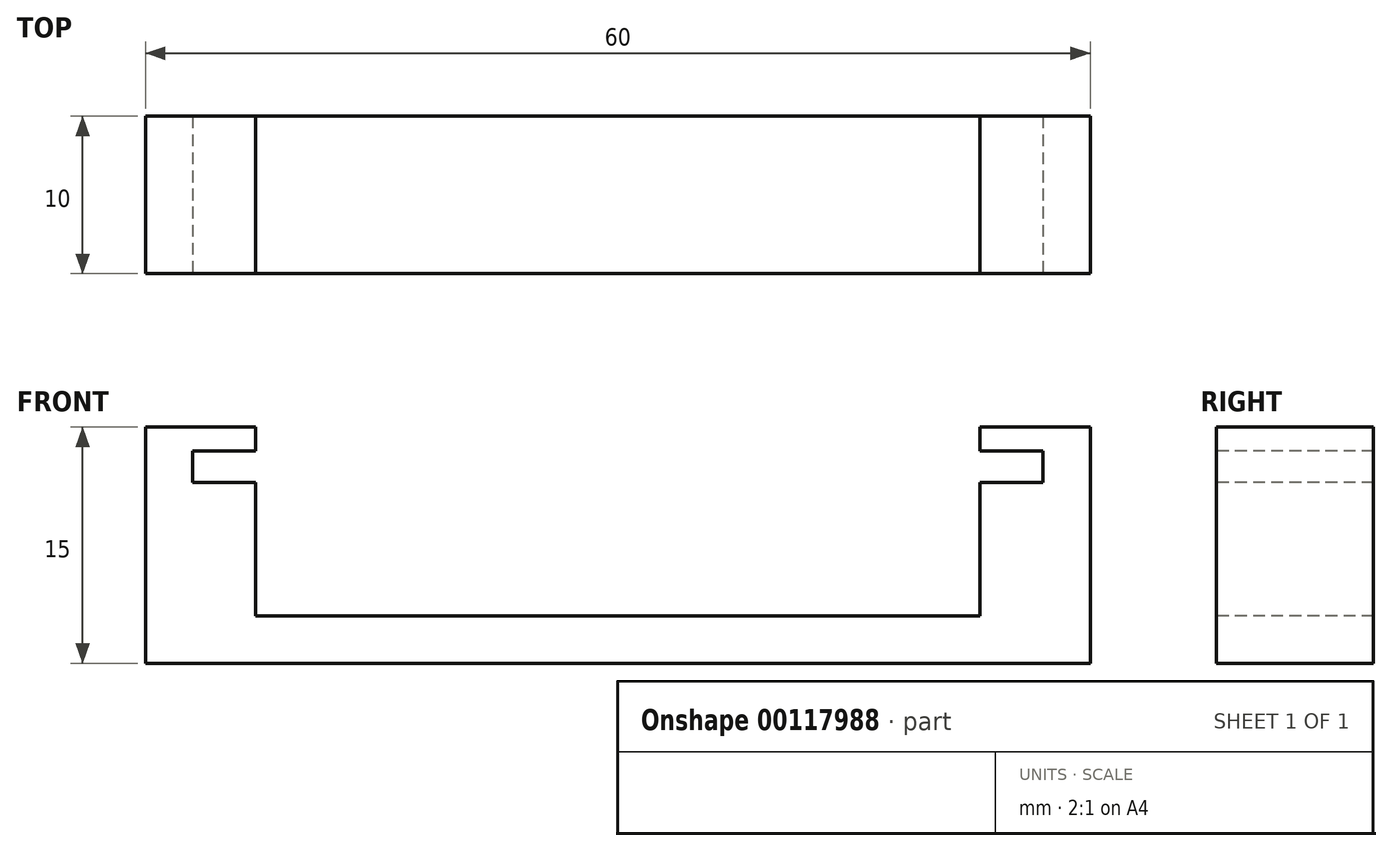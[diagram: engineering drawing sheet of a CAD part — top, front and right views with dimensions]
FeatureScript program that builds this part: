
annotation { "Feature Type Name" : "Feature", "Feature Type Description" : "" }
export const myFeature = defineFeature(function(context is Context, id is Id, definition is map)
    precondition{}
    {
        {
            var Q0;
            Q0=qCreatedBy(makeId("Top.planeOp"),FACE);
            var sketch = newSketch(context, id + "F0", { "sketchPlane" : qUnion([Q0])});
            skLineSegment(sketch, "E0.bottom", {"start": v(30, 5) * mm, "end": v(-30, 5) * mm});
            skLineSegment(sketch, "E0.top", {"start": v(30, -5) * mm, "end": v(-30, -5) * mm});
            skLineSegment(sketch, "E0.left", {"start": v(30, 5) * mm, "end": v(30, -5) * mm});
            skLineSegment(sketch, "E0.right", {"start": v(-30, 5) * mm, "end": v(-30, -5) * mm});
            skPoint(sketch, "E0.middle", {"position": v(0, 0) * mm});
            skSolve(sketch);
        }
        {
            var Q0;
            Q0=makeQuery(id+"F0.imprint","IMPRINT",FACE,{"disambiguationData":[TD([[makeQuery(id+"F0.imprint","IMPRINT",EDGE,{"derivedFrom":sQuery(id+"F0.wireOp",EDGE,"E0.bottom")}),1.0]])]});
            extrude(context, id + "F1", {"entities" : qUnion([Q0]), "depth" : 15 * mm});
        }
        {
            var Q0;
            Q0=makeQuery(id+"F1.opExtrude","SWEPT_FACE",FACE,{"disambiguationData":[OSD([sQuery(id+"F0.wireOp",EDGE,"E0.top")])]});
            var sketch = newSketch(context, id + "F2", { "sketchPlane" : qUnion([Q0])});
            skLineSegment(sketch, "E1.bottom", {"start": v(-23, 15) * mm, "end": v(23, 15) * mm});
            skLineSegment(sketch, "E1.top", {"start": v(-23, 3) * mm, "end": v(23, 3) * mm});
            skLineSegment(sketch, "E1.left", {"start": v(-23, 15) * mm, "end": v(-23, 3) * mm});
            skLineSegment(sketch, "E1.right", {"start": v(23, 15) * mm, "end": v(23, 3) * mm});
            skPoint(sketch, "E1.middle", {"position": v(0, 9) * mm});
            skLineSegment(sketch, "E2.bottom", {"start": v(-23, 13.5) * mm, "end": v(-27, 13.5) * mm});
            skLineSegment(sketch, "E2.top", {"start": v(-23, 11.5) * mm, "end": v(-27, 11.5) * mm});
            skLineSegment(sketch, "E2.left", {"start": v(-23, 13.5) * mm, "end": v(-23, 11.5) * mm});
            skLineSegment(sketch, "E2.right", {"start": v(-27, 13.5) * mm, "end": v(-27, 11.5) * mm});
            skLineSegment(sketch, "E3", {"start": v(0, 3) * mm, "end": v(0, 15) * mm, "construction": true});
            skLineSegment(sketch, "E4.MirrorCS", {"start": v(23, 13.5) * mm, "end": v(27, 13.5) * mm});
            skLineSegment(sketch, "E5.MirrorCS", {"start": v(27, 13.5) * mm, "end": v(27, 11.5) * mm});
            skLineSegment(sketch, "E6.MirrorCS", {"start": v(23, 11.5) * mm, "end": v(27, 11.5) * mm});
            skSolve(sketch);
        }
        {
            var Q0;
            {var subQ3=sQuery(id+"F2.wireOp",EDGE,"E1.bottom");Q0=makeQuery(id+"F2.imprint","IMPRINT",FACE,{"disambiguationData":[TD([[makeQuery(id+"F2.imprint","IMPRINT",EDGE,{"derivedFrom":subQ3}),1.0]])]});}
            var Q1;
            Q1=makeQuery(id+"F2.imprint","IMPRINT",FACE,{"disambiguationData":[TD([[makeQuery(id+"F2.imprint","IMPRINT",EDGE,{"derivedFrom":sQuery(id+"F2.wireOp",EDGE,"E2.bottom")}),1.0]])]});
            var Q2;
            {var subQ0=sQuery(id+"F2.wireOp",EDGE,"E4.MirrorCS");Q2=makeQuery(id+"F2.imprint","IMPRINT",FACE,{"disambiguationData":[TD([[makeQuery(id+"F2.imprint","IMPRINT",EDGE,{"derivedFrom":subQ0}),-1.0]])]});}
            extrude(context, id + "F3", {"entities" : qUnion([Q0, Q1, Q2]), "operationType" : NewBodyOperationType.REMOVE, "endBound" : BoundingType.THROUGH_ALL, "oppositeDirection" : true, "depth" : 25 * mm});
        }
    });
